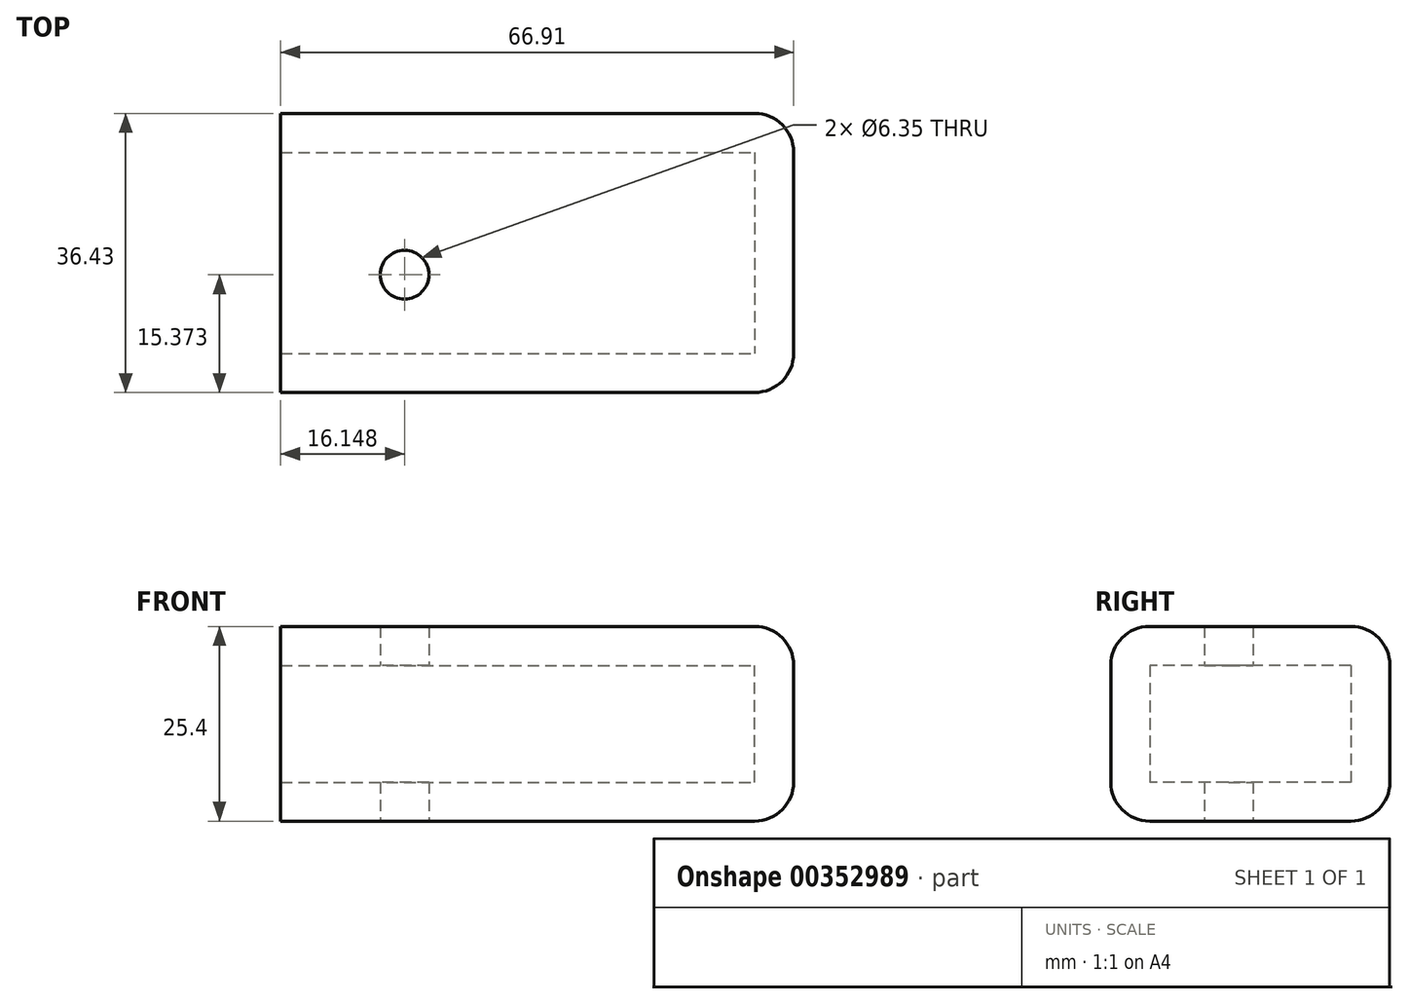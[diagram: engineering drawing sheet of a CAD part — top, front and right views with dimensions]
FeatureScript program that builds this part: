
annotation { "Feature Type Name" : "Feature", "Feature Type Description" : "" }
export const myFeature = defineFeature(function(context is Context, id is Id, definition is map)
    precondition{}
    {
        {
            var Q0;
            Q0=qCreatedBy(makeId("Top.planeOp"),FACE);
            var sketch = newSketch(context, id + "F0", { "sketchPlane" : qUnion([Q0])});
            skLineSegment(sketch, "E0.bottom", {"start": v(-27.32, 10.66) * mm, "end": v(39.59, 10.66) * mm});
            skLineSegment(sketch, "E0.top", {"start": v(-27.32, -25.77) * mm, "end": v(39.59, -25.77) * mm});
            skLineSegment(sketch, "E0.left", {"start": v(-27.32, 10.66) * mm, "end": v(-27.32, -25.77) * mm});
            skLineSegment(sketch, "E0.right", {"start": v(39.59, 10.66) * mm, "end": v(39.59, -25.77) * mm});
            skSolve(sketch);
        }
        {
            var Q0;
            Q0=makeQuery(id+"F0.imprint","IMPRINT",FACE,{"disambiguationData":[TD([[makeQuery(id+"F0.imprint","IMPRINT",EDGE,{"derivedFrom":sQuery(id+"F0.wireOp",EDGE,"E0.bottom")}),-1.0]])]});
            extrude(context, id + "F1", {"entities" : qUnion([Q0]), "depth" : 25.4 * mm});
        }
        {
            var Q0;
            Q0=makeQuery(id+"F1.opExtrude","CAP_EDGE",EDGE,{"disambiguationData":[OSD([sQuery(id+"F0.wireOp",EDGE,"E0.bottom")])],"isStart":false});
            fillet(context, id + "F2", {"entities" : qUnion([Q0]), "radius" : 5.08 * mm, "tangentPropagation" : true, "allowEdgeOverflow" : false});
        }
        {
            var Q0;
            Q0=makeQuery(id+"F1.opExtrude","CAP_EDGE",EDGE,{"disambiguationData":[OSD([sQuery(id+"F0.wireOp",EDGE,"E0.bottom")])],"isStart":true});
            fillet(context, id + "F3", {"entities" : qUnion([Q0]), "radius" : 5.08 * mm, "tangentPropagation" : true, "allowEdgeOverflow" : false});
        }
        {
            var Q0;
            Q0=makeQuery(id+"F1.opExtrude","CAP_EDGE",EDGE,{"disambiguationData":[OSD([sQuery(id+"F0.wireOp",EDGE,"E0.top")])],"isStart":false});
            fillet(context, id + "F4", {"entities" : qUnion([Q0]), "radius" : 5.08 * mm, "tangentPropagation" : true, "allowEdgeOverflow" : false});
        }
        {
            var Q0;
            Q0=makeQuery(id+"F1.opExtrude","CAP_EDGE",EDGE,{"disambiguationData":[OSD([sQuery(id+"F0.wireOp",EDGE,"E0.top")])],"isStart":true});
            fillet(context, id + "F5", {"entities" : qUnion([Q0]), "radius" : 5.08 * mm, "tangentPropagation" : true, "allowEdgeOverflow" : false});
        }
        {
            var Q0;
            Q0=makeQuery(id+"F1.opExtrude","CAP_EDGE",EDGE,{"disambiguationData":[OSD([sQuery(id+"F0.wireOp",EDGE,"E0.right")])],"isStart":true});
            var Q1;
            Q1=makeQuery(id+"F3.opFillet","BLEND_EDGE",EDGE,{"blendedFrom":[makeQuery(id+"F1.opExtrude","CAP_EDGE",EDGE,{"disambiguationData":[OSD([sQuery(id+"F0.wireOp",EDGE,"E0.bottom")])],"isStart":true}),makeQuery(id+"F1.opExtrude","SWEPT_FACE",FACE,{"disambiguationData":[OSD([sQuery(id+"F0.wireOp",EDGE,"E0.right")])]})],"blendedInto":[makeQuery(id+"F1.opExtrude","SWEPT_FACE",FACE,{"disambiguationData":[OSD([sQuery(id+"F0.wireOp",EDGE,"E0.right")])]})]});
            var Q2;
            Q2=makeQuery(id+"F2.opFillet","BLEND_EDGE",EDGE,{"blendedFrom":[makeQuery(id+"F1.opExtrude","CAP_EDGE",EDGE,{"disambiguationData":[OSD([sQuery(id+"F0.wireOp",EDGE,"E0.bottom")])],"isStart":false}),makeQuery(id+"F1.opExtrude","SWEPT_FACE",FACE,{"disambiguationData":[OSD([sQuery(id+"F0.wireOp",EDGE,"E0.right")])]})],"blendedInto":[makeQuery(id+"F1.opExtrude","SWEPT_FACE",FACE,{"disambiguationData":[OSD([sQuery(id+"F0.wireOp",EDGE,"E0.right")])]})]});
            var Q3;
            Q3=makeQuery(id+"F1.opExtrude","SWEPT_EDGE",EDGE,{"disambiguationData":[OSD([sQuery(id+"F0.wireOp",EDGE,"E0.bottom"),sQuery(id+"F0.wireOp",EDGE,"E0.right")])]});
            var Q4;
            Q4=makeQuery(id+"F1.opExtrude","CAP_EDGE",EDGE,{"disambiguationData":[OSD([sQuery(id+"F0.wireOp",EDGE,"E0.right")])],"isStart":false});
            var Q5;
            Q5=makeQuery(id+"F5.opFillet","BLEND_EDGE",EDGE,{"blendedFrom":[makeQuery(id+"F1.opExtrude","CAP_EDGE",EDGE,{"disambiguationData":[OSD([sQuery(id+"F0.wireOp",EDGE,"E0.top")])],"isStart":true}),makeQuery(id+"F1.opExtrude","SWEPT_FACE",FACE,{"disambiguationData":[OSD([sQuery(id+"F0.wireOp",EDGE,"E0.right")])]})],"blendedInto":[makeQuery(id+"F1.opExtrude","SWEPT_FACE",FACE,{"disambiguationData":[OSD([sQuery(id+"F0.wireOp",EDGE,"E0.right")])]})]});
            var Q6;
            Q6=makeQuery(id+"F1.opExtrude","SWEPT_EDGE",EDGE,{"disambiguationData":[OSD([sQuery(id+"F0.wireOp",EDGE,"E0.top"),sQuery(id+"F0.wireOp",EDGE,"E0.right")])]});
            var Q7;
            Q7=makeQuery(id+"F1.opExtrude","SWEPT_FACE",FACE,{"disambiguationData":[OSD([sQuery(id+"F0.wireOp",EDGE,"E0.right")])]});
            fillet(context, id + "F6", {"entities" : qUnion([Q0, Q1, Q2, Q3, Q4, Q5, Q6, Q7]), "radius" : 5.08 * mm, "tangentPropagation" : true, "allowEdgeOverflow" : false});
        }
        {
            var Q0;
            Q0=makeQuery(id+"F1.opExtrude","SWEPT_FACE",FACE,{"disambiguationData":[OSD([sQuery(id+"F0.wireOp",EDGE,"E0.left")])]});
            shell(context, id + "F7", {"entities" : qUnion([Q0]), "thickness" : 5.08 * mm});
        }
        {
            var Q0;
            Q0=makeQuery(id+"F1.opExtrude","CAP_FACE",FACE,{"disambiguationData":[OSD([sQuery(id+"F0.wireOp",EDGE,"E0.bottom"),sQuery(id+"F0.wireOp",EDGE,"E0.top"),sQuery(id+"F0.wireOp",EDGE,"E0.left"),sQuery(id+"F0.wireOp",EDGE,"E0.right")])],"isStart":true});
            var sketch = newSketch(context, id + "F8", { "sketchPlane" : qUnion([Q0])});
            skCircle(sketch, "E1", {"center": v(-11.17, 10.4) * mm, "radius": 3.03 * mm});
            skSolve(sketch);
        }
        {
            var Q0;
            Q0=sQuery(id+"F8.wireOp",VERTEX,"E1.center");
            var Q1;
            Q1=makeQuery(id+"F1.opExtrude","SWEPT_BODY",BODY,{"disambiguationData":[OSD([sQuery(id+"F0.wireOp",EDGE,"E0.bottom"),sQuery(id+"F0.wireOp",EDGE,"E0.top"),sQuery(id+"F0.wireOp",EDGE,"E0.left"),sQuery(id+"F0.wireOp",EDGE,"E0.right")])]});
            hole(context, id + "F9", {"style" : HoleStyle.SIMPLE, "endStyle" : HoleEndStyle.THROUGH, "standardTappedOrClearance" : lookupTablePath({ "standard" : "Benutzerdefiniert" }), "standardBlindInLast" : lookupTablePath({ "standard" : "Benutzerdefiniert" }), "holeDiameter" : 6.35 * mm, "isTappedThrough" : true, "tappedDepth" : 12.7 * mm, "tapClearance" : 3, "locations" : qUnion([Q0]), "scope" : qUnion([Q1])});
        }
    });
